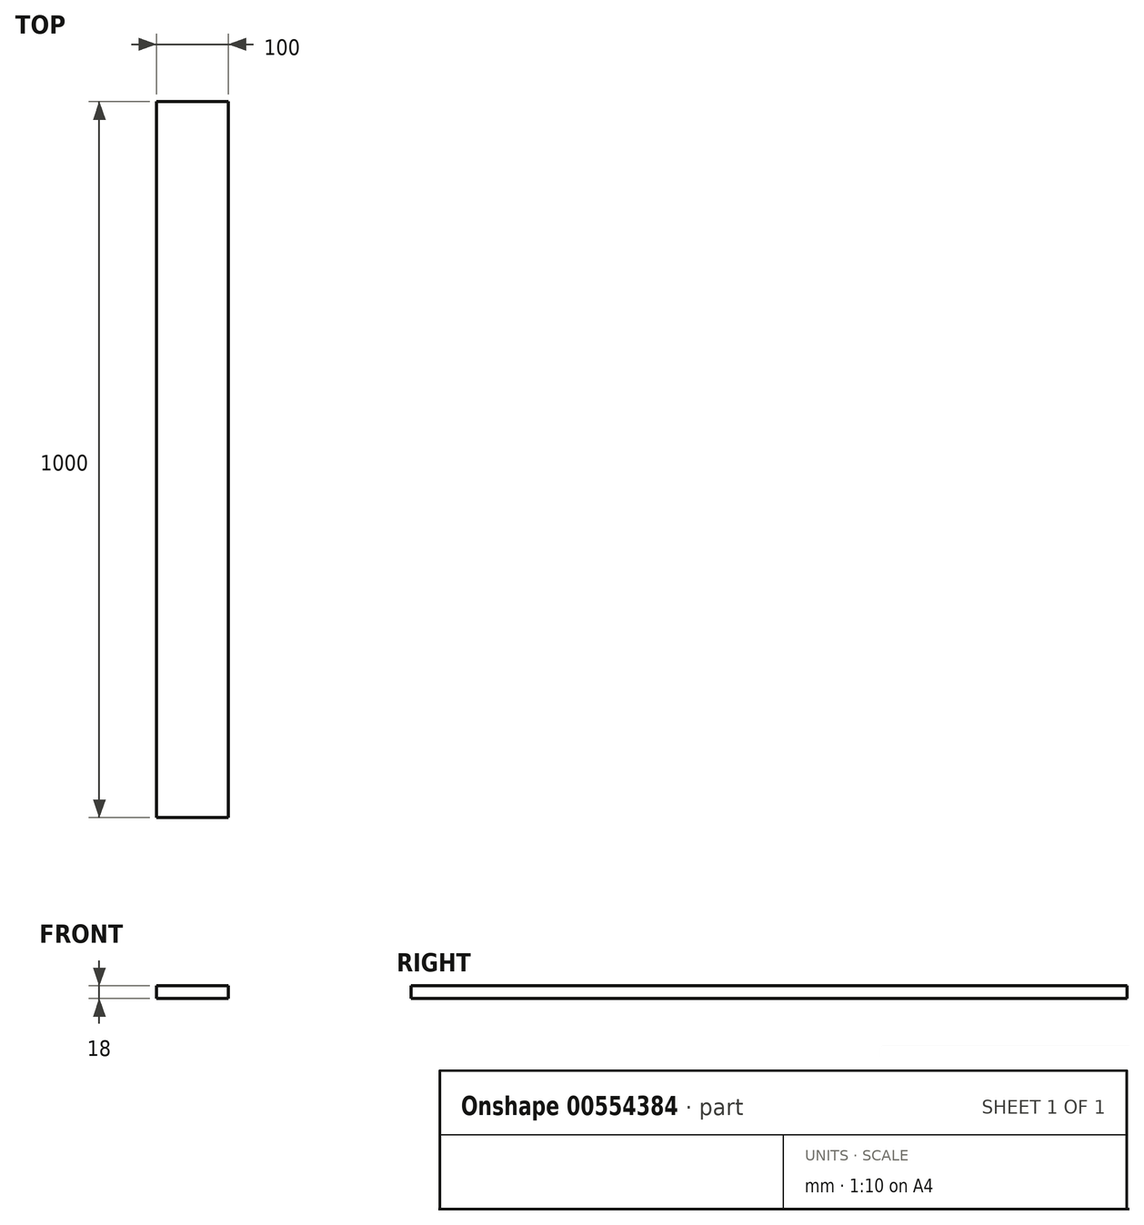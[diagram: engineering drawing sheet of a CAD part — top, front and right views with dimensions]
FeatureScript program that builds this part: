
annotation { "Feature Type Name" : "Feature", "Feature Type Description" : "" }
export const myFeature = defineFeature(function(context is Context, id is Id, definition is map)
    precondition{}
    {
        {
            var Q0;
            Q0=qCreatedBy(makeId("Top.planeOp"),FACE);
            var sketch = newSketch(context, id + "F0", { "sketchPlane" : qUnion([Q0])});
            skLineSegment(sketch, "E0.bottom", {"start": v(0, 0) * mm, "end": v(100, 0) * mm});
            skLineSegment(sketch, "E0.top", {"start": v(0, 1000) * mm, "end": v(100, 1000) * mm});
            skLineSegment(sketch, "E0.left", {"start": v(0, 0) * mm, "end": v(0, 1000) * mm});
            skLineSegment(sketch, "E0.right", {"start": v(100, 0) * mm, "end": v(100, 1000) * mm});
            skSolve(sketch);
        }
        {
            var Q0;
            Q0=makeQuery(id+"F0.imprint","IMPRINT",FACE,{"disambiguationData":[TD([[makeQuery(id+"F0.imprint","IMPRINT",EDGE,{"derivedFrom":sQuery(id+"F0.wireOp",EDGE,"E0.bottom")}),1.0]])]});
            extrude(context, id + "F1", {"entities" : qUnion([Q0]), "depth" : 18 * mm, "offsetDistance" : 25 * mm});
        }
    });
